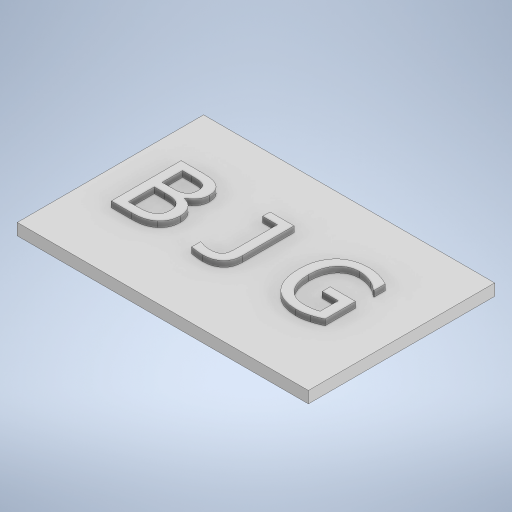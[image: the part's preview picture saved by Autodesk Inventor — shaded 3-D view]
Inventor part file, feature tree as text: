
AUTODESK INVENTOR PART (.ipt)
format: ipt  version: 2023 (Build 270158000, 158)  size: 313,856 bytes
history: native  units: in
note: dims shown in document units (in); Inventor stores cm internally (conversion verified against a paired STEP export)
features: sketch x2, extrude x1, emboss x1
ambient origin geometry x8: Origin, YZ Plane, XZ Plane, XY Plane, X Axis, Y Axis, Z Axis, Center Point
bodies: Solid1 (feature_tree)
feature tree (4):
  extrude  "Extrusion1"  Depth=6.2992in
  emboss  "Emboss2"
  sketch  "Sketch1"  dims[d0=9.8425in d1=6.2992in]
  sketch  "Sketch5"  dims[d2=0.3937in d3=0.0in d6=0.1969in d7=0.0in]
